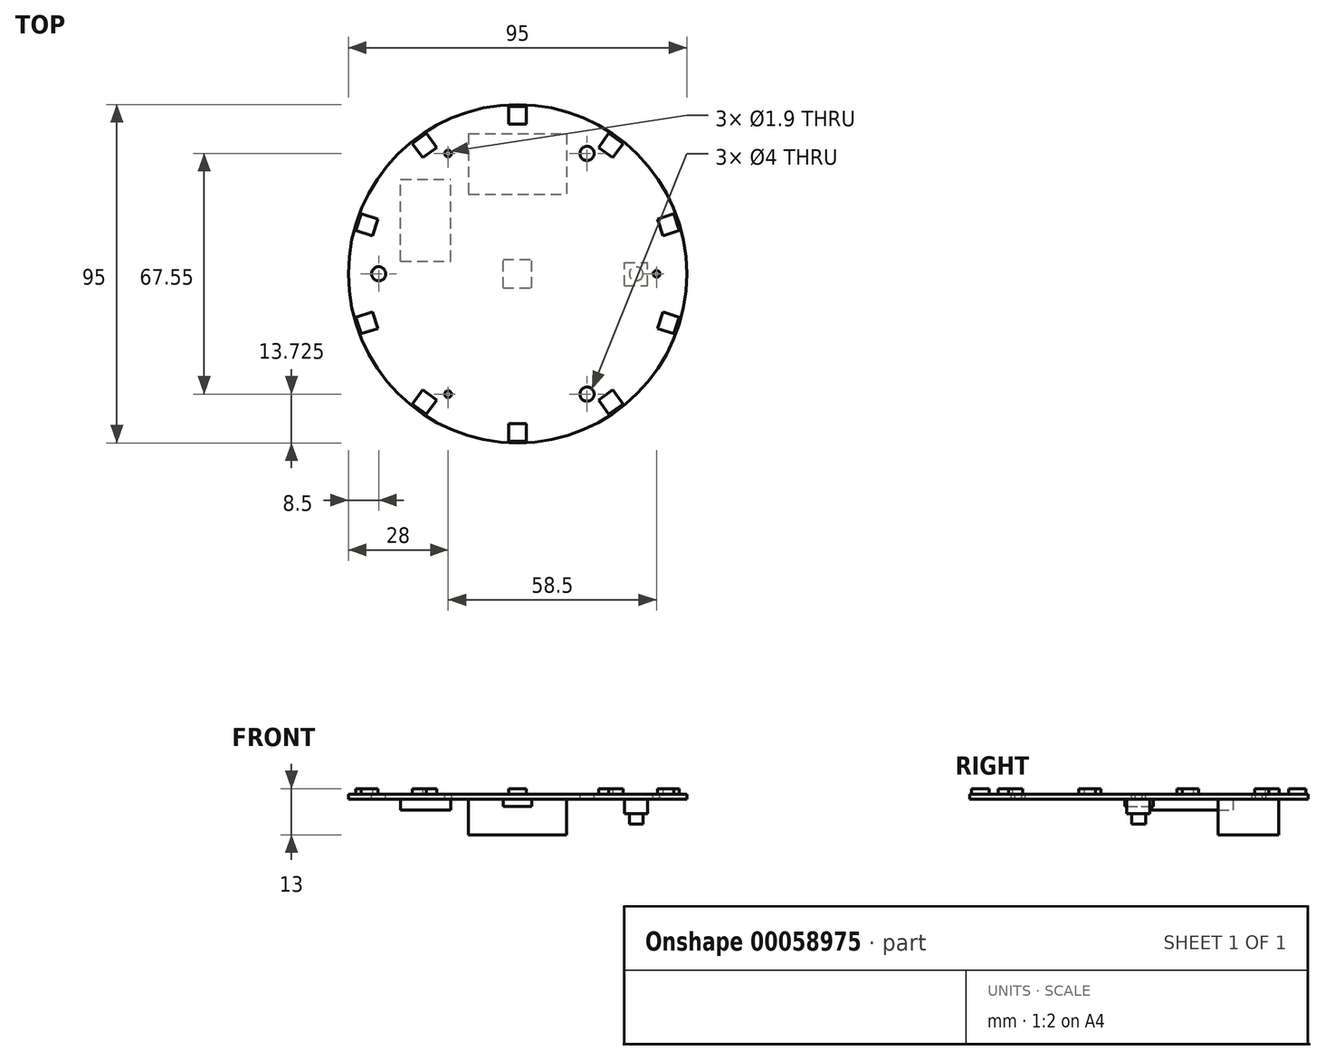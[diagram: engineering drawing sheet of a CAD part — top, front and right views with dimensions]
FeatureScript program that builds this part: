
annotation { "Feature Type Name" : "Feature", "Feature Type Description" : "" }
export const myFeature = defineFeature(function(context is Context, id is Id, definition is map)
    precondition{}
    {
        {
            var Q0;
            Q0=qCreatedBy(makeId("Top.planeOp"),FACE);
            var sketch = newSketch(context, id + "F0", { "sketchPlane" : qUnion([Q0])});
            skCircle(sketch, "E0", {"center": v(0, 0) * mm, "radius": 47.5 * mm});
            skSolve(sketch);
        }
        {
            var Q0;
            Q0=qSketchRegion(id+"F0",true);
            extrude(context, id + "F1", {"entities" : qUnion([Q0]), "depth" : 1.4 * mm});
        }
        {
            var Q0;
            Q0=makeQuery(id+"F1.opExtrude","CAP_FACE",FACE,{"disambiguationData":[OSD([sQuery(id+"F0.wireOp",EDGE,"E0")])],"isStart":false});
            var sketch = newSketch(context, id + "F2", { "sketchPlane" : qUnion([Q0])});
            skLineSegment(sketch, "E1.rect.bottom", {"start": v(27.5, 19.3) * mm, "end": v(-27.5, 19.3) * mm});
            skLineSegment(sketch, "E1.rect.top", {"start": v(27.5, -19.3) * mm, "end": v(-27.5, -19.3) * mm});
            skLineSegment(sketch, "E1.rect.left", {"start": v(27.5, 19.3) * mm, "end": v(27.5, -19.3) * mm});
            skLineSegment(sketch, "E1.rect.right", {"start": v(-27.5, 19.3) * mm, "end": v(-27.5, -19.3) * mm});
            skPoint(sketch, "E1.rect.middle", {"position": v(0, 0) * mm});
            skCircle(sketch, "E2", {"center": v(-23.4, 15.21) * mm, "radius": 4.04 * mm});
            skPoint(sketch, "E2.first.point", {"position": v(-23.05, 19.24) * mm});
            skPoint(sketch, "E2.second.point", {"position": v(-27.44, 15.27) * mm});
            skPoint(sketch, "E2.third.point", {"position": v(-25.92, 18.38) * mm});
            skCircle(sketch, "E3.MirrorC", {"center": v(-23.4, -15.21) * mm, "radius": 4.04 * mm});
            skCircle(sketch, "E4.MirrorC", {"center": v(23.4, -15.21) * mm, "radius": 4.04 * mm});
            skCircle(sketch, "E5.MirrorC", {"center": v(23.4, 15.21) * mm, "radius": 4.04 * mm});
            skSolve(sketch);
        }
        {
            var Q0;
            Q0=makeQuery(id+"F1.opExtrude","CAP_FACE",FACE,{"disambiguationData":[OSD([sQuery(id+"F0.wireOp",EDGE,"E0")])],"isStart":false});
            var sketch = newSketch(context, id + "F3", { "sketchPlane" : qUnion([Q0])});
            skLineSegment(sketch, "E6.rect.bottom", {"start": v(2.45, 46.95) * mm, "end": v(-2.45, 46.95) * mm});
            skLineSegment(sketch, "E6.rect.top", {"start": v(2.45, 42.05) * mm, "end": v(-2.45, 42.05) * mm});
            skLineSegment(sketch, "E6.rect.left", {"start": v(2.45, 46.95) * mm, "end": v(2.45, 42.05) * mm});
            skLineSegment(sketch, "E6.rect.right", {"start": v(-2.45, 46.95) * mm, "end": v(-2.45, 42.05) * mm});
            skPoint(sketch, "E6.rect.middle", {"position": v(0, 44.5) * mm});
            skLineSegment(sketch, "E7.1.0", {"start": v(-25.61, 39.42) * mm, "end": v(-29.58, 36.54) * mm});
            skLineSegment(sketch, "E7.1.1", {"start": v(-25.61, 39.42) * mm, "end": v(-22.73, 35.46) * mm});
            skLineSegment(sketch, "E7.1.2", {"start": v(-22.73, 35.46) * mm, "end": v(-26.7, 32.58) * mm});
            skLineSegment(sketch, "E7.1.3", {"start": v(-29.58, 36.54) * mm, "end": v(-26.7, 32.58) * mm});
            skLineSegment(sketch, "E7.2.0", {"start": v(-43.9, 16.84) * mm, "end": v(-45.4, 12.18) * mm});
            skLineSegment(sketch, "E7.2.1", {"start": v(-43.9, 16.84) * mm, "end": v(-39.23, 15.32) * mm});
            skLineSegment(sketch, "E7.2.2", {"start": v(-39.23, 15.32) * mm, "end": v(-40.75, 10.66) * mm});
            skLineSegment(sketch, "E7.2.3", {"start": v(-45.4, 12.18) * mm, "end": v(-40.75, 10.66) * mm});
            skLineSegment(sketch, "E7.3.0", {"start": v(-45.4, -12.18) * mm, "end": v(-43.9, -16.84) * mm});
            skLineSegment(sketch, "E7.3.1", {"start": v(-45.4, -12.18) * mm, "end": v(-40.75, -10.66) * mm});
            skLineSegment(sketch, "E7.3.2", {"start": v(-40.75, -10.66) * mm, "end": v(-39.23, -15.32) * mm});
            skLineSegment(sketch, "E7.3.3", {"start": v(-43.9, -16.84) * mm, "end": v(-39.23, -15.32) * mm});
            skLineSegment(sketch, "E7.4.0", {"start": v(-29.58, -36.54) * mm, "end": v(-25.61, -39.42) * mm});
            skLineSegment(sketch, "E7.4.1", {"start": v(-29.58, -36.54) * mm, "end": v(-26.7, -32.58) * mm});
            skLineSegment(sketch, "E7.4.2", {"start": v(-26.7, -32.58) * mm, "end": v(-22.73, -35.46) * mm});
            skLineSegment(sketch, "E7.4.3", {"start": v(-25.61, -39.42) * mm, "end": v(-22.73, -35.46) * mm});
            skLineSegment(sketch, "E7.5.0", {"start": v(-2.45, -46.95) * mm, "end": v(2.45, -46.95) * mm});
            skLineSegment(sketch, "E7.5.1", {"start": v(-2.45, -46.95) * mm, "end": v(-2.45, -42.05) * mm});
            skLineSegment(sketch, "E7.5.2", {"start": v(-2.45, -42.05) * mm, "end": v(2.45, -42.05) * mm});
            skLineSegment(sketch, "E7.5.3", {"start": v(2.45, -46.95) * mm, "end": v(2.45, -42.05) * mm});
            skLineSegment(sketch, "E7.6.0", {"start": v(25.61, -39.42) * mm, "end": v(29.58, -36.54) * mm});
            skLineSegment(sketch, "E7.6.1", {"start": v(25.61, -39.42) * mm, "end": v(22.73, -35.46) * mm});
            skLineSegment(sketch, "E7.6.2", {"start": v(22.73, -35.46) * mm, "end": v(26.7, -32.58) * mm});
            skLineSegment(sketch, "E7.6.3", {"start": v(29.58, -36.54) * mm, "end": v(26.7, -32.58) * mm});
            skLineSegment(sketch, "E7.7.0", {"start": v(43.9, -16.84) * mm, "end": v(45.4, -12.18) * mm});
            skLineSegment(sketch, "E7.7.1", {"start": v(43.9, -16.84) * mm, "end": v(39.23, -15.32) * mm});
            skLineSegment(sketch, "E7.7.2", {"start": v(39.23, -15.32) * mm, "end": v(40.75, -10.66) * mm});
            skLineSegment(sketch, "E7.7.3", {"start": v(45.4, -12.18) * mm, "end": v(40.75, -10.66) * mm});
            skLineSegment(sketch, "E7.8.0", {"start": v(45.4, 12.18) * mm, "end": v(43.9, 16.84) * mm});
            skLineSegment(sketch, "E7.8.1", {"start": v(45.4, 12.18) * mm, "end": v(40.75, 10.66) * mm});
            skLineSegment(sketch, "E7.8.2", {"start": v(40.75, 10.66) * mm, "end": v(39.23, 15.32) * mm});
            skLineSegment(sketch, "E7.8.3", {"start": v(43.9, 16.84) * mm, "end": v(39.23, 15.32) * mm});
            skLineSegment(sketch, "E7.9.0", {"start": v(29.58, 36.54) * mm, "end": v(25.61, 39.42) * mm});
            skLineSegment(sketch, "E7.9.1", {"start": v(29.58, 36.54) * mm, "end": v(26.7, 32.58) * mm});
            skLineSegment(sketch, "E7.9.2", {"start": v(26.7, 32.58) * mm, "end": v(22.73, 35.46) * mm});
            skLineSegment(sketch, "E7.9.3", {"start": v(25.61, 39.42) * mm, "end": v(22.73, 35.46) * mm});
            skPoint(sketch, "E7.center", {"position": v(0, 0) * mm});
            skSolve(sketch);
        }
        {
            var Q0;
            Q0=qSketchRegion(id+"F3",true);
            extrude(context, id + "F4", {"entities" : qUnion([Q0]), "operationType" : NewBodyOperationType.ADD, "depth" : 1.6 * mm});
        }
        {
            var Q0;
            Q0=makeQuery(id+"F1.opExtrude","CAP_FACE",FACE,{"disambiguationData":[OSD([sQuery(id+"F0.wireOp",EDGE,"E0")])],"isStart":false});
            var sketch = newSketch(context, id + "F5", { "sketchPlane" : qUnion([Q0])});
            skCircle(sketch, "E8", {"center": v(-39, 0) * mm, "radius": 2 * mm});
            skCircle(sketch, "E9.1.0", {"center": v(19.5, -33.77) * mm, "radius": 2 * mm});
            skCircle(sketch, "E9.2.0", {"center": v(19.5, 33.77) * mm, "radius": 2 * mm});
            skPoint(sketch, "E9.center", {"position": v(0, 0) * mm});
            skCircle(sketch, "E10", {"center": v(39, 0) * mm, "radius": 0.95 * mm});
            skCircle(sketch, "E11.1.0", {"center": v(-19.5, 33.77) * mm, "radius": 0.95 * mm});
            skCircle(sketch, "E11.2.0", {"center": v(-19.5, -33.77) * mm, "radius": 0.95 * mm});
            skSolve(sketch);
        }
        {
            var Q0;
            Q0=qSketchRegion(id+"F5",true);
            extrude(context, id + "F6", {"entities" : qUnion([Q0]), "operationType" : NewBodyOperationType.REMOVE, "endBound" : BoundingType.THROUGH_ALL, "oppositeDirection" : true, "depth" : 25 * mm});
        }
        {
            var Q0;
            Q0=makeQuery(id+"F1.opExtrude","CAP_FACE",FACE,{"disambiguationData":[OSD([sQuery(id+"F0.wireOp",EDGE,"E0")])],"isStart":true});
            var sketch = newSketch(context, id + "F7", { "sketchPlane" : qUnion([Q0])});
            skLineSegment(sketch, "E12.rect.bottom", {"start": v(-13.75, -39.3) * mm, "end": v(13.75, -39.3) * mm});
            skLineSegment(sketch, "E12.rect.top", {"start": v(-13.75, -22.3) * mm, "end": v(13.75, -22.3) * mm});
            skLineSegment(sketch, "E12.rect.left", {"start": v(-13.75, -39.3) * mm, "end": v(-13.75, -22.3) * mm});
            skLineSegment(sketch, "E12.rect.right", {"start": v(13.75, -39.3) * mm, "end": v(13.75, -22.3) * mm});
            skPoint(sketch, "E12.rect.middle", {"position": v(0, -30.8) * mm});
            skSolve(sketch);
        }
        {
            var Q0;
            Q0=qSketchRegion(id+"F7",true);
            extrude(context, id + "F8", {"entities" : qUnion([Q0]), "operationType" : NewBodyOperationType.ADD, "depth" : 10 * mm});
        }
        {
            var Q0;
            Q0=makeQuery(id+"F1.opExtrude","CAP_FACE",FACE,{"disambiguationData":[OSD([sQuery(id+"F0.wireOp",EDGE,"E0")])],"isStart":true});
            var sketch = newSketch(context, id + "F9", { "sketchPlane" : qUnion([Q0])});
            skLineSegment(sketch, "E13.bottom", {"start": v(-32.82, -3.54) * mm, "end": v(-18.82, -3.54) * mm});
            skLineSegment(sketch, "E13.top", {"start": v(-32.82, -26.54) * mm, "end": v(-18.82, -26.54) * mm});
            skLineSegment(sketch, "E13.left", {"start": v(-32.82, -3.54) * mm, "end": v(-32.82, -26.54) * mm});
            skLineSegment(sketch, "E13.right", {"start": v(-18.82, -3.54) * mm, "end": v(-18.82, -26.54) * mm});
            skSolve(sketch);
        }
        {
            var Q0;
            Q0=qSketchRegion(id+"F9",true);
            extrude(context, id + "F10", {"entities" : qUnion([Q0]), "operationType" : NewBodyOperationType.ADD, "depth" : 3 * mm});
        }
        {
            var Q0;
            Q0=makeQuery(id+"F1.opExtrude","CAP_FACE",FACE,{"disambiguationData":[OSD([sQuery(id+"F0.wireOp",EDGE,"E0")])],"isStart":true});
            var sketch = newSketch(context, id + "F11", { "sketchPlane" : qUnion([Q0])});
            skLineSegment(sketch, "E14.bottom", {"start": v(-4.05, 3.95) * mm, "end": v(3.95, 3.95) * mm});
            skLineSegment(sketch, "E14.top", {"start": v(-4.05, -4.05) * mm, "end": v(3.95, -4.05) * mm});
            skLineSegment(sketch, "E14.left", {"start": v(-4.05, 3.95) * mm, "end": v(-4.05, -4.05) * mm});
            skLineSegment(sketch, "E14.right", {"start": v(3.95, 3.95) * mm, "end": v(3.95, -4.05) * mm});
            skSolve(sketch);
        }
        {
            var Q0;
            Q0=qSketchRegion(id+"F11",true);
            extrude(context, id + "F12", {"entities" : qUnion([Q0]), "operationType" : NewBodyOperationType.ADD, "depth" : 2 * mm});
        }
        {
            var Q0;
            Q0=makeQuery(id+"F1.opExtrude","CAP_FACE",FACE,{"disambiguationData":[OSD([sQuery(id+"F0.wireOp",EDGE,"E0")])],"isStart":true});
            var sketch = newSketch(context, id + "F13", { "sketchPlane" : qUnion([Q0])});
            skLineSegment(sketch, "E15.bottom", {"start": v(29.95, 3.35) * mm, "end": v(36.45, 3.35) * mm});
            skLineSegment(sketch, "E15.top", {"start": v(29.95, -3.15) * mm, "end": v(36.45, -3.15) * mm});
            skLineSegment(sketch, "E15.left", {"start": v(29.95, 3.35) * mm, "end": v(29.95, -3.15) * mm});
            skLineSegment(sketch, "E15.right", {"start": v(36.45, 3.35) * mm, "end": v(36.45, -3.15) * mm});
            skSolve(sketch);
        }
        {
            var Q0;
            Q0=qSketchRegion(id+"F13",true);
            extrude(context, id + "F14", {"entities" : qUnion([Q0]), "operationType" : NewBodyOperationType.ADD, "depth" : 4 * mm});
        }
        {
            var Q0;
            Q0=makeQuery(id+"F14.opExtrude","CAP_FACE",FACE,{"disambiguationData":[OSD([sQuery(id+"F13.wireOp",EDGE,"E15.bottom"),sQuery(id+"F13.wireOp",EDGE,"E15.top"),sQuery(id+"F13.wireOp",EDGE,"E15.left"),sQuery(id+"F13.wireOp",EDGE,"E15.right")])],"isStart":false});
            var sketch = newSketch(context, id + "F15", { "sketchPlane" : qUnion([Q0])});
            skCircle(sketch, "E16", {"center": v(33.29, 0) * mm, "radius": 1.93 * mm});
            skSolve(sketch);
        }
        {
            var Q0;
            Q0=qSketchRegion(id+"F15",true);
            extrude(context, id + "F16", {"entities" : qUnion([Q0]), "operationType" : NewBodyOperationType.ADD, "depth" : 3 * mm});
        }
    });
